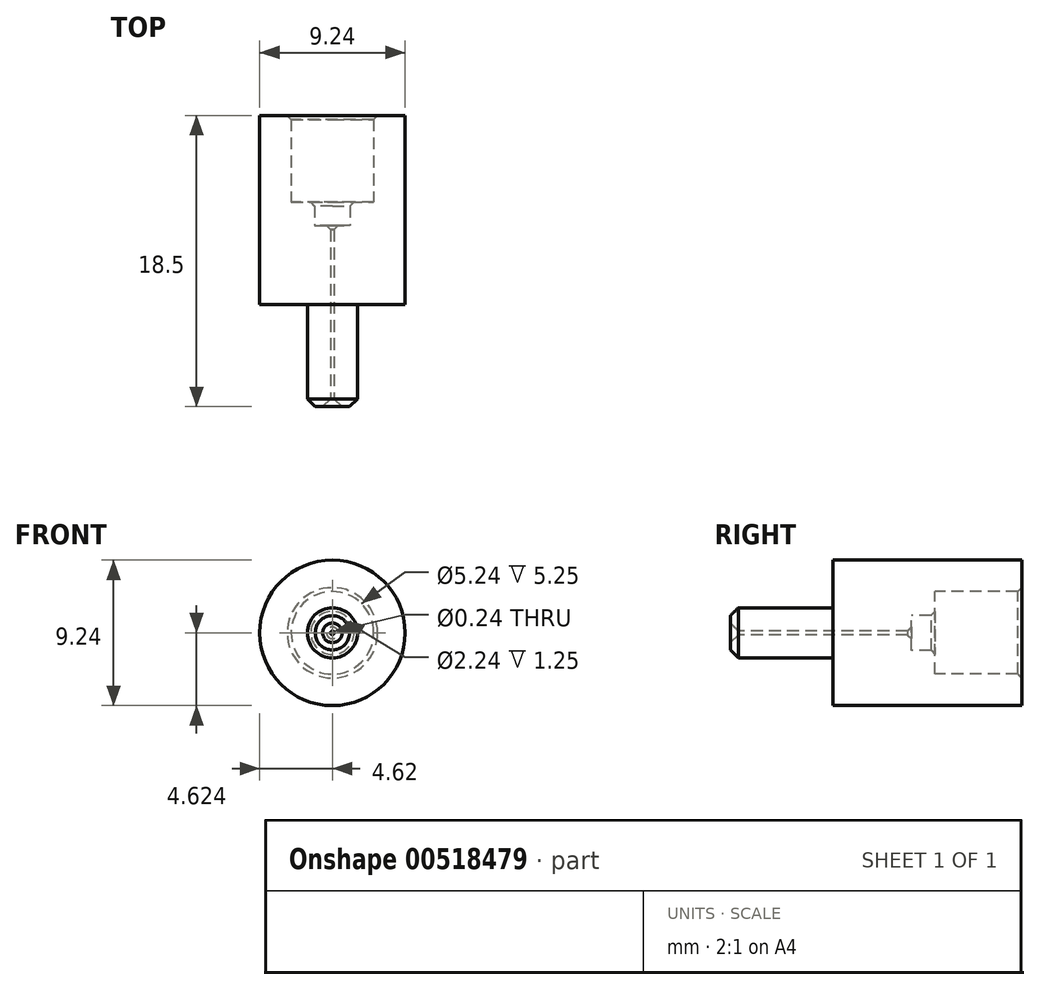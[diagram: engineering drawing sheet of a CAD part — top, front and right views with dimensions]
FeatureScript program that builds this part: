
annotation { "Feature Type Name" : "Feature", "Feature Type Description" : "" }
export const myFeature = defineFeature(function(context is Context, id is Id, definition is map)
    precondition{}
    {
        {
            var Q0;
            Q0=qCreatedBy(makeId("Right.planeOp"),FACE);
            var sketch = newSketch(context, id + "F0", { "sketchPlane" : qUnion([Q0])});
            skLineSegment(sketch, "E0", {"start": v(-10.46, -2.8) * mm, "end": v(-15.96, -2.8) * mm});
            skLineSegment(sketch, "E1", {"start": v(-15.96, -2.8) * mm, "end": v(-15.96, -4.3) * mm});
            skLineSegment(sketch, "E2", {"start": v(-15.96, -4.3) * mm, "end": v(-17.46, -4.3) * mm});
            skLineSegment(sketch, "E3", {"start": v(-17.46, -4.3) * mm, "end": v(-17.46, -5.3) * mm});
            skLineSegment(sketch, "E4", {"start": v(-17.46, -5.3) * mm, "end": v(-28.96, -5.3) * mm});
            skLineSegment(sketch, "E5", {"start": v(-10.46, -2.8) * mm, "end": v(-10.46, -0.8) * mm});
            skLineSegment(sketch, "E6", {"start": v(-10.46, -0.8) * mm, "end": v(-22.46, -0.8) * mm});
            skLineSegment(sketch, "E7", {"start": v(-22.46, -0.8) * mm, "end": v(-22.46, -3.84) * mm});
            skLineSegment(sketch, "E8", {"start": v(-22.46, -3.84) * mm, "end": v(-28.96, -3.84) * mm});
            skLineSegment(sketch, "E9", {"start": v(-28.96, -3.84) * mm, "end": v(-28.96, -5.3) * mm});
            skLineSegment(sketch, "E10", {"start": v(-28.96, -5.43) * mm, "end": v(-10.46, -5.43) * mm, "construction": true});
            skLineSegment(sketch, "E11.MirrorCS", {"start": v(-17.46, -5.55) * mm, "end": v(-28.96, -5.55) * mm, "construction": true});
            skLineSegment(sketch, "E12.MirrorCS", {"start": v(-10.46, -10.05) * mm, "end": v(-22.46, -10.05) * mm, "construction": true});
            skLineSegment(sketch, "E13.MirrorCS", {"start": v(-22.46, -7.02) * mm, "end": v(-28.96, -7.02) * mm, "construction": true});
            skLineSegment(sketch, "E14.MirrorCS", {"start": v(-10.46, -8.05) * mm, "end": v(-15.96, -8.05) * mm, "construction": true});
            skLineSegment(sketch, "E15.MirrorCS", {"start": v(-15.96, -6.55) * mm, "end": v(-17.46, -6.55) * mm, "construction": true});
            skCircle(sketch, "E16", {"center": v(-14.7, -5.43) * mm, "radius": 1.59 * mm, "construction": true});
            skSolve(sketch);
        }
        {
            var Q0;
            Q0=makeQuery(id+"F0.imprint","IMPRINT",FACE,{"disambiguationData":[TD([[makeQuery(id+"F0.imprint","IMPRINT",EDGE,{"derivedFrom":sQuery(id+"F0.wireOp",EDGE,"E0")}),-1.0]])]});
            var Q1;
            Q1=sQuery(id+"F0.wireOp",EDGE,"E10");
            revolve(context, id + "F1", {"entities" : qUnion([Q0]), "axis" : qUnion([Q1]), "revolveType" : RevolveType.FULL});
        }
        {
            var Q0;
            Q0=makeQuery(id+"F1.opRevolve","SWEPT_EDGE",EDGE,{"disambiguationData":[OSD([sQuery(id+"F0.wireOp",EDGE,"E8"),sQuery(id+"F0.wireOp",EDGE,"E9")])]});
            var Q1;
            Q1=makeQuery(id+"F1.opRevolve","SWEPT_EDGE",EDGE,{"disambiguationData":[OSD([sQuery(id+"F0.wireOp",EDGE,"E9"),sQuery(id+"F0.wireOp",EDGE,"E4")])]});
            chamfer(context, id + "F2", {"entities" : qUnion([Q0, Q1]), "width" : .5 * mm, "tangentPropagation" : true});
        }
        {
            var Q0;
            Q0=makeQuery(id+"F1.opRevolve","SWEPT_EDGE",EDGE,{"disambiguationData":[OSD([sQuery(id+"F0.wireOp",EDGE,"E1"),sQuery(id+"F0.wireOp",EDGE,"E2")])]});
            var Q1;
            Q1=makeQuery(id+"F1.opRevolve","SWEPT_EDGE",EDGE,{"disambiguationData":[OSD([sQuery(id+"F0.wireOp",EDGE,"E0"),sQuery(id+"F0.wireOp",EDGE,"E5")])]});
            var Q2;
            Q2=makeQuery(id+"F1.opRevolve","SWEPT_EDGE",EDGE,{"disambiguationData":[OSD([sQuery(id+"F0.wireOp",EDGE,"E3"),sQuery(id+"F0.wireOp",EDGE,"E4")])]});
            chamfer(context, id + "F3", {"entities" : qUnion([Q0, Q1, Q2]), "width" : .25 * mm, "tangentPropagation" : true});
        }
    });
